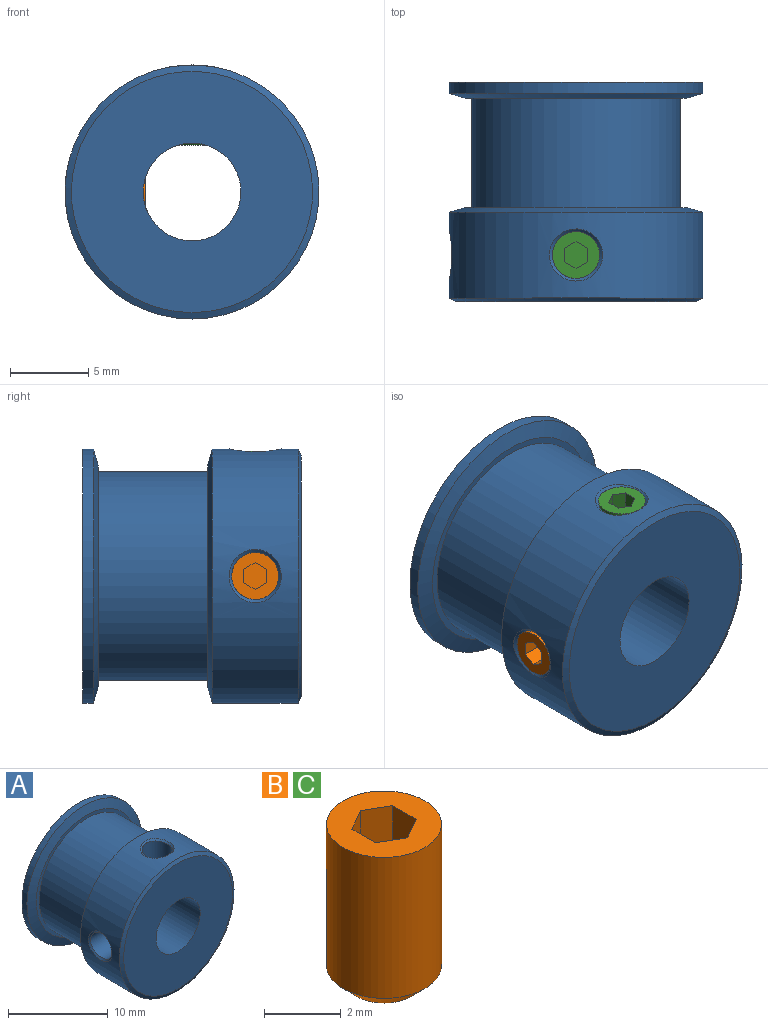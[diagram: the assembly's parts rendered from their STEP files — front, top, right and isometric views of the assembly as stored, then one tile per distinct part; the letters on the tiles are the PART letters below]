
ASSEMBLY  parts=3 mates=2
PART A: 17 faces, bbox 16.3x14x16.3 mm
  f0: cylinder r=8.12mm len=16.25mm, axis (0,-1,0), area 262.8mm2, adj f2,f3,f15,f16
  f1: plane 15.43x15.43mm, normal (0,-1,0), area 156.3mm2, adj f2,f12
  f2: cone r=8.12mm half-angle=63.4deg, axis (0,1,0), area 22.9mm2, adj f0,f1
  f3: cone r=8.12mm half-angle=74.3deg, axis (0,-1,0), area 51.6mm2, adj f0,f4
  f4: plane 14.17x14.17mm, normal (0,1,0), area 17.7mm2, adj f3,f5
  f5: cylinder r=6.68mm len=13.35mm, axis (0,-1,0), area 293.6mm2, adj f4,f6
  f6: plane 14.17x14.17mm, normal (0,-1,0), area 17.7mm2, adj f5,f7
  f7: cone r=8.12mm half-angle=73.9deg, axis (0,1,0), area 51.7mm2, adj f6,f8
  f8: cylinder r=8.12mm len=16.25mm, axis (0,-1,0), area 35.7mm2, adj f7,f9
  f9: cone r=4.87mm half-angle=86.8deg, axis (0,1,0), area 133mm2, adj f8,f10
  f10: cone r=4.79mm half-angle=23.1deg, axis (0,-1,0), area 6.1mm2, adj f9,f11
  f11: plane 9.59x9.59mm, normal (0,1,0), area 41.6mm2, adj f10,f12
  f12: cylinder r=3.12mm len=14mm, axis (0,-1,0), area 260.3mm2, adj f1,f11,f13,f14
  f13: cylinder r=1.5mm len=5.04mm, axis (0,0,-1), area 47.5mm2, adj f12,f15
  f14: cylinder r=1.5mm len=5.04mm, axis (1,0,0), area 47.5mm2, adj f12,f16
  f15: bspline ~3.4x3.33mm, area 2.5mm2, adj f0,f13
  f16: bspline ~3.4x3.33mm, area 2.5mm2, adj f0,f14
PART B: 11 faces, bbox 3x3x5 mm
  f0: plane 3x3mm, normal (0,0,1), area 5.1mm2, adj f1,f3,f4,f5,f6,f7,f8
  f1: cylinder r=1.5mm len=4.5mm, axis (0,0,-1), area 42.4mm2, adj f0,f10
  f2: plane 2x2mm, normal (0,0,-1), area 3.1mm2, adj f10
  f3: plane 1.5x0.87mm, normal (-1,0,0), area 1.3mm2, adj f0,f4,f8,f9
  f4: plane 1.5x0.75mm, normal (-0.5,-0.87,0), area 1.3mm2, adj f0,f3,f5,f9
  f5: plane 1.5x0.75mm, normal (0.5,-0.87,0), area 1.3mm2, adj f0,f4,f6,f9
  f6: plane 1.5x0.87mm, normal (1,0,0), area 1.3mm2, adj f0,f5,f7,f9
  f7: plane 1.5x0.75mm, normal (0.5,0.87,0), area 1.3mm2, adj f0,f6,f8,f9
  f8: plane 1.5x0.75mm, normal (-0.5,0.87,0), area 1.3mm2, adj f0,f3,f7,f9
  f9: plane 1.73x1.5mm, normal (0,0,1), area 1.9mm2, adj f3,f4,f5,f6,f7,f8
  f10: cone r=1.5mm half-angle=45deg, axis (0,0,1), area 5.6mm2, adj f1,f2
PART C: same geometry as B
PLACE A at identity
PLACE B rot(axis=(-0.58,-0.58,0.58),120deg) t=(-2.99,2.96,0)mm
PLACE C t=(0,2.96,2.99)mm
MATE fastened C.f1 <-> A.f13  axis (0,0,-1) through (0,2.96,7.99)mm
MATE fastened B.f1 <-> A.f14  axis (1,0,0) through (-7.99,2.96,0)mm
